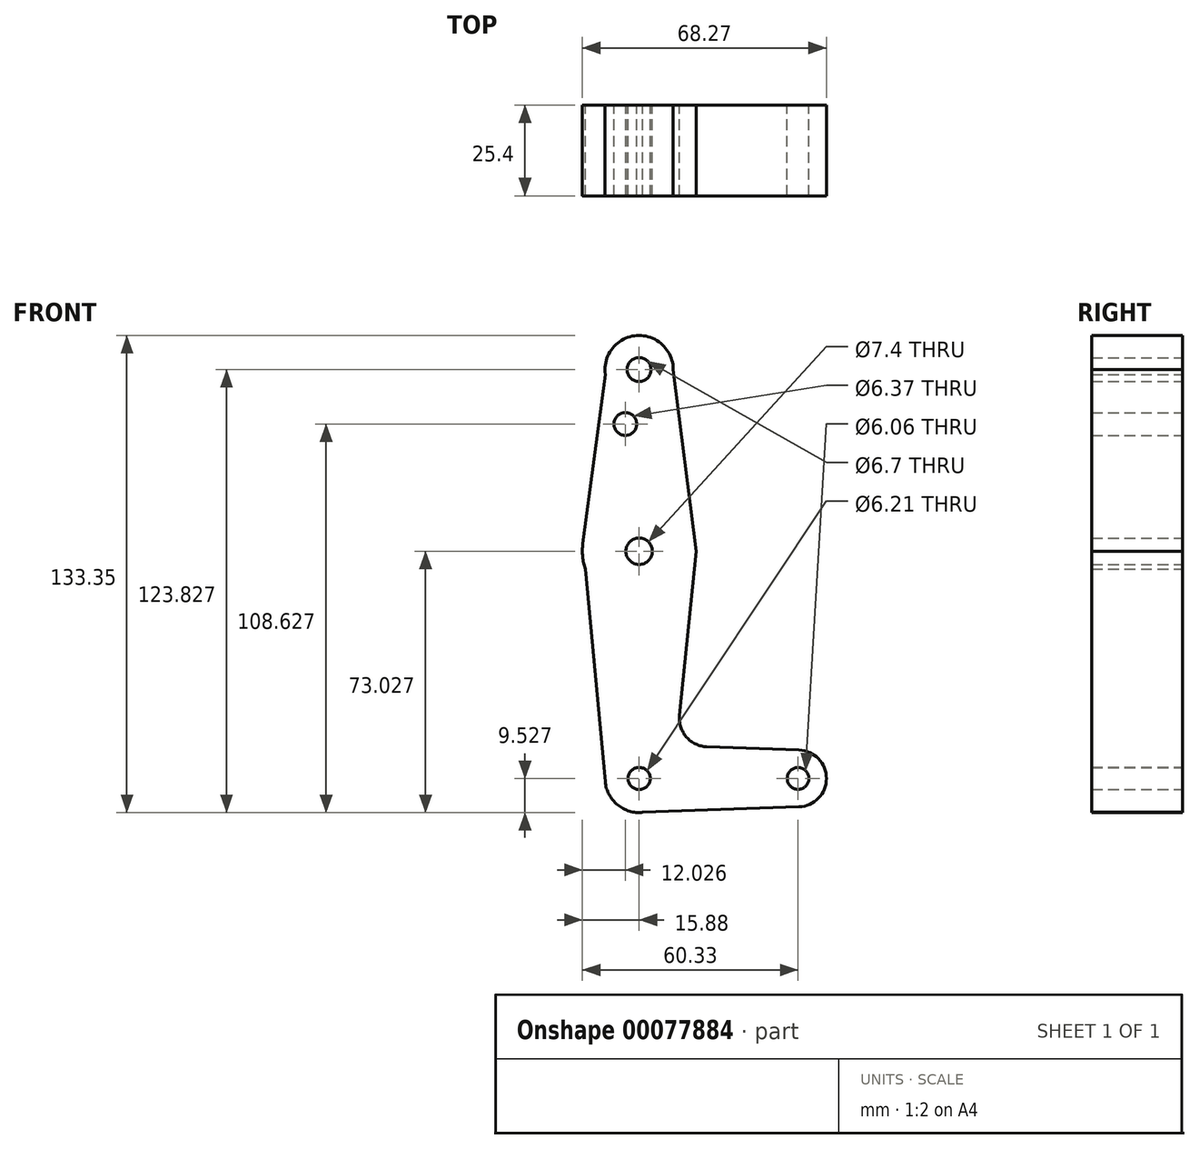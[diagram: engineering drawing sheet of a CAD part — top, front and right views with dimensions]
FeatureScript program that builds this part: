
annotation { "Feature Type Name" : "Feature", "Feature Type Description" : "" }
export const myFeature = defineFeature(function(context is Context, id is Id, definition is map)
    precondition{}
    {
        {
            var Q0;
            Q0=qCreatedBy(makeId("Front.planeOp"),FACE);
            var sketch = newSketch(context, id + "F0", { "sketchPlane" : qUnion([Q0])});
            skLineSegment(sketch, "E0", {"start": v(-21.74, 55.88) * mm, "end": v(-21.74, -58.42) * mm});
            skLineSegment(sketch, "E1", {"start": v(-21.74, -58.42) * mm, "end": v(22.7, -58.42) * mm});
            skCircle(sketch, "E2", {"center": v(-21.74, 55.88) * mm, "radius": 9.53 * mm});
            skCircle(sketch, "E3", {"center": v(-21.74, 5.08) * mm, "radius": 15.88 * mm});
            skCircle(sketch, "E4", {"center": v(-21.74, -58.42) * mm, "radius": 9.53 * mm});
            skCircle(sketch, "E5", {"center": v(22.7, -58.42) * mm, "radius": 7.94 * mm});
            skLineSegment(sketch, "E6", {"start": v(-2.8, -49.57) * mm, "end": v(23, -50.5) * mm});
            skLineSegment(sketch, "E7", {"start": v(-22.1, -67.94) * mm, "end": v(22.99, -66.36) * mm});
            skLineSegment(sketch, "E8", {"start": v(-31.17, 54.52) * mm, "end": v(-37.48, 7.17) * mm});
            skLineSegment(sketch, "E9", {"start": v(-12.22, 55.88) * mm, "end": v(-5.74, 5.08) * mm});
            skLineSegment(sketch, "E10", {"start": v(-37.48, 7.17) * mm, "end": v(-31.17, -59.9) * mm});
            skCircle(sketch, "E11", {"center": v(-25.6, 40.68) * mm, "radius": 3.19 * mm});
            skCircle(sketch, "E12", {"center": v(-21.74, 5.08) * mm, "radius": 3.7 * mm});
            skCircle(sketch, "E13", {"center": v(-21.74, 55.88) * mm, "radius": 3.35 * mm});
            skCircle(sketch, "E14", {"center": v(-21.74, -58.42) * mm, "radius": 3.1 * mm});
            skCircle(sketch, "E15", {"center": v(22.7, -58.42) * mm, "radius": 3.03 * mm});
            skLineSegment(sketch, "E16", {"start": v(-10.42, -40.82) * mm, "end": v(-5.74, 5.08) * mm});
            skArc(sketch, "E17.filletArc", {"start": v(-10.42, -40.82) * mm, "mid": v(-8.5, -46.85) * mm, "end": v(-2.8, -49.57) * mm});
            skSolve(sketch);
        }
        {
            var Q0;
            Q0 = qSketchRegion(id + "F0", true);
            var Q1;
            {var subQ0=sQuery(id+"F0.wireOp",EDGE,"E4");var subQ1=sQuery(id+"F0.wireOp",EDGE,"E0");var subQ2=makeQuery(id+"F0.imprint","INTERSECT",VERTEX,{"derivedFrom":[subQ1,subQ0]});Q1=makeQuery(id+"F0.imprint","IMPRINT",FACE,{"disambiguationData":[TD([[makeQuery(id+"F0.imprint","IMPRINT",EDGE,{"disambiguationData":[TD([[subQ2,-1.0]])],"derivedFrom":subQ1}),1.0]])]});}
            extrude(context, id + "F1", {"entities" : qUnion([Q0, Q1]), "depth" : 25.4 * mm});
        }
    });
